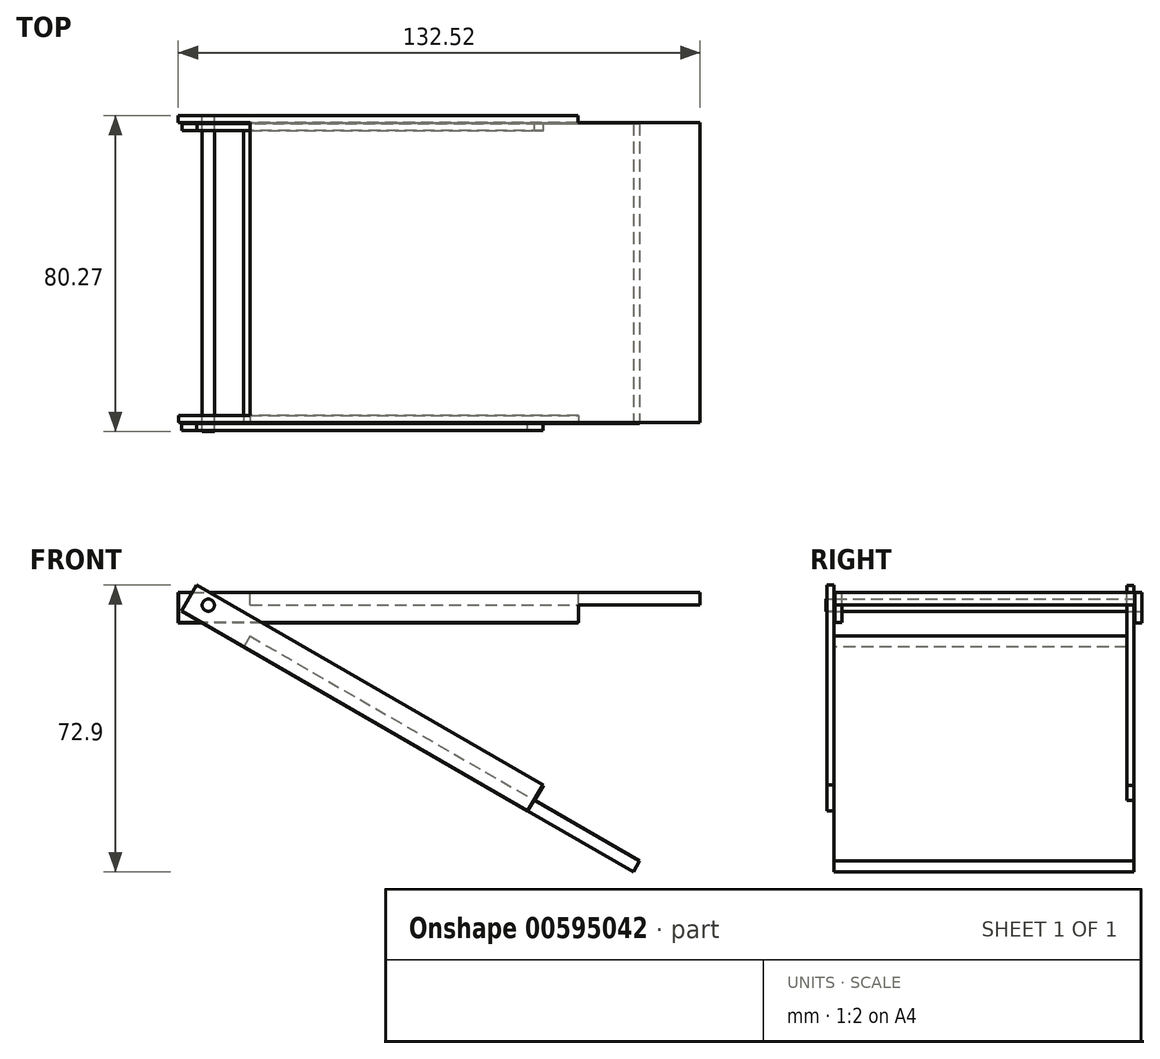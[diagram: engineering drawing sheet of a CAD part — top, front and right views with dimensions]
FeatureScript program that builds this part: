
annotation { "Feature Type Name" : "Feature", "Feature Type Description" : "" }
export const myFeature = defineFeature(function(context is Context, id is Id, definition is map)
    precondition{}
    {
        {
            var Q0;
            Q0=qCreatedBy(makeId("Top.planeOp"),FACE);
            var sketch = newSketch(context, id + "F0", { "sketchPlane" : qUnion([Q0])});
            skLineSegment(sketch, "E0.bottom", {"start": v(0, 0) * mm, "end": v(114.3, 0) * mm});
            skLineSegment(sketch, "E0.top", {"start": v(0, 76.2) * mm, "end": v(114.3, 76.2) * mm});
            skLineSegment(sketch, "E0.left", {"start": v(0, 0) * mm, "end": v(0, 76.2) * mm});
            skLineSegment(sketch, "E0.right", {"start": v(114.3, 0) * mm, "end": v(114.3, 76.2) * mm});
            skSolve(sketch);
        }
        {
            var Q0;
            Q0=makeQuery(id+"F0.imprint","IMPRINT",FACE,{"disambiguationData":[TD([[makeQuery(id+"F0.imprint","IMPRINT",EDGE,{"derivedFrom":sQuery(id+"F0.wireOp",EDGE,"E0.bottom")}),1.0]])]});
            extrude(context, id + "F1", {"entities" : qUnion([Q0]), "depth" : 3.17 * mm, "offsetDistance" : 25.4 * mm});
        }
        {
            var Q0;
            Q0=makeQuery(id+"F1.opExtrude","SWEPT_FACE",FACE,{"disambiguationData":[OSD([sQuery(id+"F0.wireOp",EDGE,"E0.bottom")])]});
            var sketch = newSketch(context, id + "F2", { "sketchPlane" : qUnion([Q0])});
            skLineSegment(sketch, "E1.bottom", {"start": v(83.46, 3.18) * mm, "end": v(-18.14, 3.18) * mm});
            skLineSegment(sketch, "E1.top", {"start": v(83.46, -4.44) * mm, "end": v(-18.14, -4.44) * mm});
            skLineSegment(sketch, "E1.left", {"start": v(83.46, 3.18) * mm, "end": v(83.46, -4.44) * mm});
            skLineSegment(sketch, "E1.right", {"start": v(-18.14, 3.18) * mm, "end": v(-18.14, -4.44) * mm});
            skSolve(sketch);
        }
        {
            var Q0;
            Q0 = qSketchRegion(id + "F2", true);
            extrude(context, id + "F3", {"entities" : qUnion([Q0]), "operationType" : NewBodyOperationType.ADD, "oppositeDirection" : true, "depth" : 1.78 * mm, "offsetDistance" : 25.4 * mm});
        }
        {
            var Q0;
            Q0=makeQuery(id+"F1.opExtrude","SWEPT_FACE",FACE,{"disambiguationData":[OSD([sQuery(id+"F0.wireOp",EDGE,"E0.top")])]});
            var sketch = newSketch(context, id + "F4", { "sketchPlane" : qUnion([Q0])});
            skLineSegment(sketch, "E2.bottom", {"start": v(-83.29, 3.18) * mm, "end": v(18.22, 3.18) * mm});
            skLineSegment(sketch, "E2.top", {"start": v(-83.29, -4.5) * mm, "end": v(18.22, -4.5) * mm});
            skLineSegment(sketch, "E2.left", {"start": v(-83.29, 3.18) * mm, "end": v(-83.29, -4.5) * mm});
            skLineSegment(sketch, "E2.right", {"start": v(18.22, 3.18) * mm, "end": v(18.22, -4.5) * mm});
            skSolve(sketch);
        }
        {
            var Q0;
            Q0 = qSketchRegion(id + "F4", true);
            extrude(context, id + "F5", {"entities" : qUnion([Q0]), "operationType" : NewBodyOperationType.ADD, "depth" : 1.78 * mm, "offsetDistance" : 25.4 * mm});
        }
        {
            var Q0;
            Q0=makeQuery(id+"F1.opExtrude","SWEPT_BODY",BODY,{"disambiguationData":[OSD([sQuery(id+"F0.wireOp",EDGE,"E0.bottom"),sQuery(id+"F0.wireOp",EDGE,"E0.top"),sQuery(id+"F0.wireOp",EDGE,"E0.left"),sQuery(id+"F0.wireOp",EDGE,"E0.right")])]});
            var Q1;
            Q1=makeQuery(id+"F1.opExtrude","CAP_EDGE",EDGE,{"disambiguationData":[OSD([sQuery(id+"F0.wireOp",EDGE,"E0.left")])],"isStart":false});
            transform(context, id + "F6", {"entities" : qUnion([Q0]), "transformType" : TransformType.ROTATION, "transformAxis" : qUnion([Q1]), "angle" : 0 * degree, "makeCopy" : false});
        }
        {
            var Q0;
            Q0=makeQuery(id+"F5.opExtrude","CAP_FACE",FACE,{"disambiguationData":[OSD([sQuery(id+"F4.wireOp",EDGE,"E2.bottom"),sQuery(id+"F4.wireOp",EDGE,"E2.top"),sQuery(id+"F4.wireOp",EDGE,"E2.left"),sQuery(id+"F4.wireOp",EDGE,"E2.right")])],"isStart":false});
            var sketch = newSketch(context, id + "F7", { "sketchPlane" : qUnion([Q0])});
            skCircle(sketch, "E3", {"center": v(14.33, 0) * mm, "radius": 1.6 * mm});
            skSolve(sketch);
        }
        {
            var Q0;
            Q0=makeQuery(id+"F1.opExtrude","SWEPT_BODY",BODY,{"disambiguationData":[OSD([sQuery(id+"F0.wireOp",EDGE,"E0.bottom"),sQuery(id+"F0.wireOp",EDGE,"E0.top"),sQuery(id+"F0.wireOp",EDGE,"E0.left"),sQuery(id+"F0.wireOp",EDGE,"E0.right")])]});
            transform(context, id + "F8", {"entities" : qUnion([Q0]), "transformType" : TransformType.TRANSLATION_3D, "dx" : 0 * mm, "dy" : -74.42 * mm, "dz" : -60.2 * mm, "makeCopy" : true});
        }
        {
            var Q0;
            Q0=makeQuery(id+"F8.opPattern","COPY",BODY,{"derivedFrom":makeQuery(id+"F1.opExtrude","SWEPT_BODY",BODY,{"disambiguationData":[OSD([sQuery(id+"F0.wireOp",EDGE,"E0.bottom"),sQuery(id+"F0.wireOp",EDGE,"E0.top"),sQuery(id+"F0.wireOp",EDGE,"E0.left"),sQuery(id+"F0.wireOp",EDGE,"E0.right")])]}),"instanceName":"1"});
            var Q1;
            Q1=makeQuery(id+"F8.opPattern","COPY",EDGE,{"derivedFrom":makeQuery(id+"F5.opExtrude","CAP_EDGE",EDGE,{"disambiguationData":[OSD([sQuery(id+"F4.wireOp",EDGE,"E2.bottom")])],"isStart":false}),"instanceName":"1"});
            transform(context, id + "F9", {"entities" : qUnion([Q0]), "transformType" : TransformType.ROTATION, "transformAxis" : qUnion([Q1]), "angle" : 180 * degree, "oppositeDirection" : true, "makeCopy" : false});
        }
        {
            var Q0;
            Q0=makeQuery(id+"F8.opPattern","COPY",BODY,{"derivedFrom":makeQuery(id+"F1.opExtrude","SWEPT_BODY",BODY,{"disambiguationData":[OSD([sQuery(id+"F0.wireOp",EDGE,"E0.bottom"),sQuery(id+"F0.wireOp",EDGE,"E0.top"),sQuery(id+"F0.wireOp",EDGE,"E0.left"),sQuery(id+"F0.wireOp",EDGE,"E0.right")])]}),"instanceName":"1"});
            var Q1;
            Q1=makeQuery(id+"F8.opPattern","COPY",EDGE,{"derivedFrom":makeQuery(id+"F1.opExtrude","CAP_EDGE",EDGE,{"disambiguationData":[OSD([sQuery(id+"F0.wireOp",EDGE,"E0.left")])],"isStart":true}),"instanceName":"1"});
            transform(context, id + "F10", {"entities" : qUnion([Q0]), "transformType" : TransformType.ROTATION, "transformAxis" : qUnion([Q1]), "angle" : 30 * degree, "oppositeDirection" : true, "makeCopy" : false});
        }
        {
            var Q0;
            Q0=makeQuery(id+"F8.opPattern","COPY",BODY,{"derivedFrom":makeQuery(id+"F1.opExtrude","SWEPT_BODY",BODY,{"disambiguationData":[OSD([sQuery(id+"F0.wireOp",EDGE,"E0.bottom"),sQuery(id+"F0.wireOp",EDGE,"E0.top"),sQuery(id+"F0.wireOp",EDGE,"E0.left"),sQuery(id+"F0.wireOp",EDGE,"E0.right")])]}),"instanceName":"1"});
            var Q1;
            Q1=makeQuery(id+"F8.opPattern","COPY",FACE,{"derivedFrom":makeQuery(id+"F1.opExtrude","CAP_FACE",FACE,{"disambiguationData":[OSD([sQuery(id+"F0.wireOp",EDGE,"E0.bottom"),sQuery(id+"F0.wireOp",EDGE,"E0.top"),sQuery(id+"F0.wireOp",EDGE,"E0.left"),sQuery(id+"F0.wireOp",EDGE,"E0.right")])],"isStart":true}),"instanceName":"1"});
            transform(context, id + "F11", {"entities" : qUnion([Q0]), "transformType" : TransformType.TRANSLATION_3D, "dx" : 0 * mm, "dy" : -5.6 * mm, "dz" : 45.97 * mm, "makeCopy" : false});
        }
        {
            var Q0;
            Q0=makeQuery(id+"F7.imprint","IMPRINT",FACE,{"disambiguationData":[TD([[makeQuery(id+"F7.imprint","IMPRINT",EDGE,{"derivedFrom":sQuery(id+"F7.wireOp",EDGE,"E3")}),-1.0]])]});
            var sketch = newSketch(context, id + "F12", { "sketchPlane" : qUnion([Q0])});
            skCircle(sketch, "E4", {"center": v(10.6, 0) * mm, "radius": 1.56 * mm});
            skSolve(sketch);
        }
        {
            var Q0;
            Q0 = qSketchRegion(id + "F12", true);
            extrude(context, id + "F13", {"entities" : qUnion([Q0]), "oppositeDirection" : true, "depth" : 80.26 * mm, "offsetDistance" : 25.4 * mm});
        }
    });
